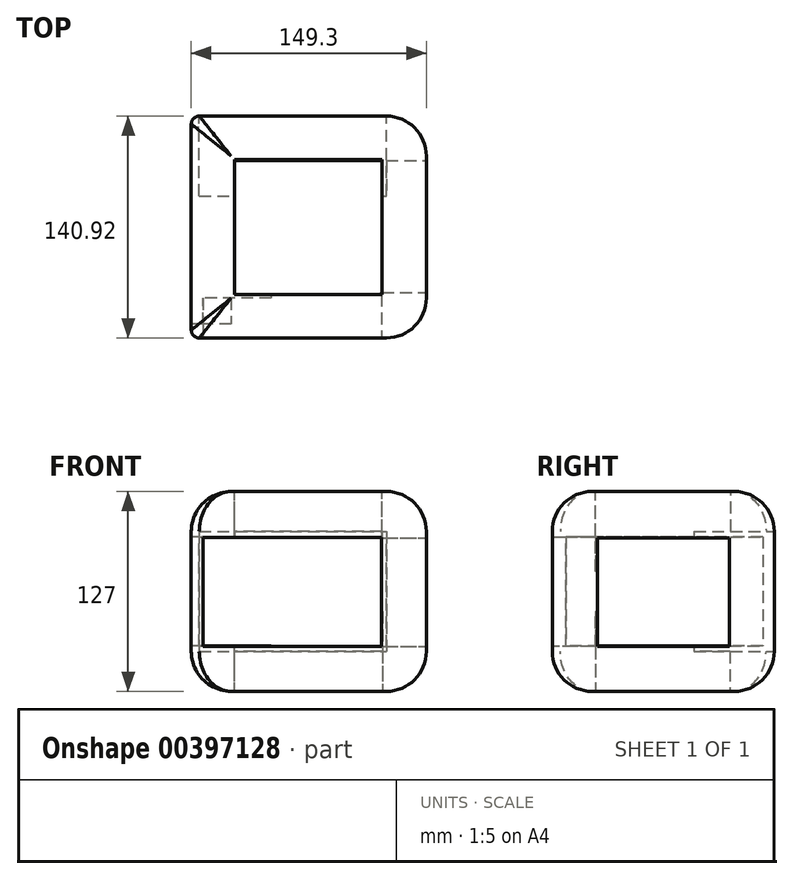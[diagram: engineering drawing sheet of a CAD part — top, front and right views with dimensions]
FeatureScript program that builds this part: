
annotation { "Feature Type Name" : "Feature", "Feature Type Description" : "" }
export const myFeature = defineFeature(function(context is Context, id is Id, definition is map)
    precondition{}
    {
        {
            var Q0;
            Q0=qCreatedBy(makeId("Top.planeOp"),FACE);
            var sketch = newSketch(context, id + "F0", { "sketchPlane" : qUnion([Q0])});
            skLineSegment(sketch, "E0.bottom", {"start": v(-73.46, -68.51) * mm, "end": v(75.84, -68.51) * mm});
            skLineSegment(sketch, "E0.top", {"start": v(-73.46, 72.4) * mm, "end": v(75.84, 72.4) * mm});
            skLineSegment(sketch, "E0.left", {"start": v(-73.46, -68.51) * mm, "end": v(-73.46, 72.4) * mm});
            skLineSegment(sketch, "E0.right", {"start": v(75.84, -68.51) * mm, "end": v(75.84, 72.4) * mm});
            skSolve(sketch);
        }
        {
            var Q0;
            Q0 = qSketchRegion(id + "F0", true);
            extrude(context, id + "F1", {"entities" : qUnion([Q0]), "depth" : 127 * mm});
        }
        {
            var Q0;
            Q0=makeQuery(id+"F1.opExtrude","CAP_EDGE",EDGE,{"disambiguationData":[OSD([sQuery(id+"F0.wireOp",EDGE,"E0.right")])],"isStart":false});
            var Q1;
            Q1=makeQuery(id+"F1.opExtrude","CAP_EDGE",EDGE,{"disambiguationData":[OSD([sQuery(id+"F0.wireOp",EDGE,"E0.top")])],"isStart":false});
            var Q2;
            Q2=makeQuery(id+"F1.opExtrude","CAP_EDGE",EDGE,{"disambiguationData":[OSD([sQuery(id+"F0.wireOp",EDGE,"E0.left")])],"isStart":false});
            var Q3;
            Q3=makeQuery(id+"F1.opExtrude","CAP_EDGE",EDGE,{"disambiguationData":[OSD([sQuery(id+"F0.wireOp",EDGE,"E0.bottom")])],"isStart":false});
            var Q4;
            Q4=makeQuery(id+"F1.opExtrude","CAP_EDGE",EDGE,{"disambiguationData":[OSD([sQuery(id+"F0.wireOp",EDGE,"E0.top")])],"isStart":true});
            var Q5;
            Q5=makeQuery(id+"F1.opExtrude","SWEPT_FACE",FACE,{"disambiguationData":[OSD([sQuery(id+"F0.wireOp",EDGE,"E0.right")])]});
            var Q6;
            Q6=makeQuery(id+"F1.opExtrude","CAP_EDGE",EDGE,{"disambiguationData":[OSD([sQuery(id+"F0.wireOp",EDGE,"E0.bottom")])],"isStart":true});
            var Q7;
            Q7=makeQuery(id+"F1.opExtrude","CAP_EDGE",EDGE,{"disambiguationData":[OSD([sQuery(id+"F0.wireOp",EDGE,"E0.left")])],"isStart":true});
            fillet(context, id + "F2", {"entities" : qUnion([Q0, Q1, Q2, Q3, Q4, Q5, Q6, Q7]), "radius" : 25.4 * mm, "tangentPropagation" : true, "allowEdgeOverflow" : false});
        }
        {
            var Q0;
            Q0=makeQuery(id+"F2.opFillet","BLEND_EDGE",EDGE,{"blendedFrom":[makeQuery(id+"F1.opExtrude","CAP_EDGE",EDGE,{"disambiguationData":[OSD([sQuery(id+"F0.wireOp",EDGE,"E0.top")])],"isStart":false}),makeQuery(id+"F1.opExtrude","CAP_EDGE",EDGE,{"disambiguationData":[OSD([sQuery(id+"F0.wireOp",EDGE,"E0.left")])],"isStart":false})],"blendedInto":[]});
            var Q1;
            Q1=makeQuery(id+"F2.opFillet","BLEND_EDGE",EDGE,{"blendedFrom":[makeQuery(id+"F1.opExtrude","CAP_EDGE",EDGE,{"disambiguationData":[OSD([sQuery(id+"F0.wireOp",EDGE,"E0.bottom")])],"isStart":false}),makeQuery(id+"F1.opExtrude","CAP_EDGE",EDGE,{"disambiguationData":[OSD([sQuery(id+"F0.wireOp",EDGE,"E0.left")])],"isStart":false})],"blendedInto":[]});
            var Q2;
            {var subQ0=sQuery(id+"F0.wireOp",EDGE,"E0.left");Q2=makeQuery(id+"F2.opFillet","BLEND_EDGE",EDGE,{"blendedFrom":[makeQuery(id+"F1.opExtrude","CAP_EDGE",EDGE,{"disambiguationData":[OSD([subQ0])],"isStart":false}),makeQuery(id+"F1.opExtrude","SWEPT_FACE",FACE,{"disambiguationData":[OSD([subQ0])]})],"blendedInto":[makeQuery(id+"F1.opExtrude","SWEPT_FACE",FACE,{"disambiguationData":[OSD([subQ0])]})]});}
            var Q3;
            {var subQ0=sQuery(id+"F0.wireOp",EDGE,"E0.top");Q3=makeQuery(id+"F2.opFillet","BLEND_EDGE",EDGE,{"blendedFrom":[makeQuery(id+"F1.opExtrude","CAP_EDGE",EDGE,{"disambiguationData":[OSD([subQ0])],"isStart":false}),makeQuery(id+"F1.opExtrude","SWEPT_FACE",FACE,{"disambiguationData":[OSD([subQ0])]})],"blendedInto":[makeQuery(id+"F1.opExtrude","SWEPT_FACE",FACE,{"disambiguationData":[OSD([subQ0])]})]});}
            fillet(context, id + "F3", {"entities" : qUnion([Q0, Q1, Q2, Q3]), "radius" : 5.08 * mm, "tangentPropagation" : true, "allowEdgeOverflow" : false});
        }
        {
            var Q0;
            Q0=makeQuery(id+"F1.opExtrude","CAP_FACE",FACE,{"disambiguationData":[OSD([sQuery(id+"F0.wireOp",EDGE,"E0.bottom"),sQuery(id+"F0.wireOp",EDGE,"E0.top"),sQuery(id+"F0.wireOp",EDGE,"E0.left"),sQuery(id+"F0.wireOp",EDGE,"E0.right")])],"isStart":false});
            var sketch = newSketch(context, id + "F4", { "sketchPlane" : qUnion([Q0])});
            skLineSegment(sketch, "E1.bottom", {"start": v(-46, 44.95) * mm, "end": v(47.65, 44.95) * mm});
            skLineSegment(sketch, "E1.top", {"start": v(-46, -40.95) * mm, "end": v(47.65, -40.95) * mm});
            skLineSegment(sketch, "E1.left", {"start": v(-46, 44.95) * mm, "end": v(-46, -40.95) * mm});
            skLineSegment(sketch, "E1.right", {"start": v(47.65, 44.95) * mm, "end": v(47.65, -40.95) * mm});
            skSolve(sketch);
        }
        {
            var Q0;
            Q0 = qSketchRegion(id + "F4", true);
            extrude(context, id + "F5", {"entities" : qUnion([Q0]), "operationType" : NewBodyOperationType.REMOVE, "oppositeDirection" : true, "depth" : 25.4 * mm});
        }
        {
            var Q0;
            Q0=makeQuery(id+"F1.opExtrude","CAP_FACE",FACE,{"disambiguationData":[OSD([sQuery(id+"F0.wireOp",EDGE,"E0.bottom"),sQuery(id+"F0.wireOp",EDGE,"E0.top"),sQuery(id+"F0.wireOp",EDGE,"E0.left"),sQuery(id+"F0.wireOp",EDGE,"E0.right")])],"isStart":true});
            var sketch = newSketch(context, id + "F6", { "sketchPlane" : qUnion([Q0])});
            skLineSegment(sketch, "E2.bottom", {"start": v(-46.24, 40.95) * mm, "end": v(47.89, 40.95) * mm});
            skLineSegment(sketch, "E2.top", {"start": v(-46.24, -44.24) * mm, "end": v(47.89, -44.24) * mm});
            skLineSegment(sketch, "E2.left", {"start": v(-46.24, 40.95) * mm, "end": v(-46.24, -44.24) * mm});
            skLineSegment(sketch, "E2.right", {"start": v(47.89, 40.95) * mm, "end": v(47.89, -44.24) * mm});
            skSolve(sketch);
        }
        {
            var Q0;
            Q0 = qSketchRegion(id + "F6", true);
            extrude(context, id + "F7", {"entities" : qUnion([Q0]), "operationType" : NewBodyOperationType.REMOVE, "oppositeDirection" : true, "depth" : 25.4 * mm});
        }
        {
            var Q0;
            Q0=makeQuery(id+"F1.opExtrude","SWEPT_FACE",FACE,{"disambiguationData":[OSD([sQuery(id+"F0.wireOp",EDGE,"E0.left")])]});
            var sketch = newSketch(context, id + "F8", { "sketchPlane" : qUnion([Q0])});
            skLineSegment(sketch, "E3.bottom", {"start": v(-65.1, 98.2) * mm, "end": v(59.77, 98.2) * mm});
            skLineSegment(sketch, "E3.top", {"start": v(-65.1, 28.85) * mm, "end": v(59.77, 28.85) * mm});
            skLineSegment(sketch, "E3.left", {"start": v(-65.1, 98.2) * mm, "end": v(-65.1, 28.85) * mm});
            skLineSegment(sketch, "E3.right", {"start": v(59.77, 98.2) * mm, "end": v(59.77, 28.85) * mm});
            skSolve(sketch);
        }
        {
            var Q0;
            Q0 = qSketchRegion(id + "F8", true);
            extrude(context, id + "F9", {"entities" : qUnion([Q0]), "operationType" : NewBodyOperationType.REMOVE, "oppositeDirection" : true, "depth" : 25.4 * mm});
        }
        {
            var Q0;
            Q0=makeQuery(id+"F1.opExtrude","SWEPT_FACE",FACE,{"disambiguationData":[OSD([sQuery(id+"F0.wireOp",EDGE,"E0.bottom")])]});
            var sketch = newSketch(context, id + "F10", { "sketchPlane" : qUnion([Q0])});
            skLineSegment(sketch, "E4.bottom", {"start": v(-66.05, 97.88) * mm, "end": v(47.54, 97.88) * mm});
            skLineSegment(sketch, "E4.top", {"start": v(-66.05, 28.54) * mm, "end": v(47.54, 28.54) * mm});
            skLineSegment(sketch, "E4.left", {"start": v(-66.05, 97.88) * mm, "end": v(-66.05, 28.54) * mm});
            skLineSegment(sketch, "E4.right", {"start": v(47.54, 97.88) * mm, "end": v(47.54, 28.54) * mm});
            skSolve(sketch);
        }
        {
            var Q0;
            Q0 = qSketchRegion(id + "F10", true);
            extrude(context, id + "F11", {"entities" : qUnion([Q0]), "operationType" : NewBodyOperationType.REMOVE, "oppositeDirection" : true, "depth" : 25.4 * mm});
        }
        {
            var Q0;
            Q0=makeQuery(id+"F1.opExtrude","SWEPT_FACE",FACE,{"disambiguationData":[OSD([sQuery(id+"F0.wireOp",EDGE,"E0.right")])]});
            var sketch = newSketch(context, id + "F12", { "sketchPlane" : qUnion([Q0])});
            skLineSegment(sketch, "E5.bottom", {"start": v(-39.7, 97.57) * mm, "end": v(44.08, 97.57) * mm});
            skLineSegment(sketch, "E5.top", {"start": v(-39.7, 28.54) * mm, "end": v(44.08, 28.54) * mm});
            skLineSegment(sketch, "E5.left", {"start": v(-39.7, 97.57) * mm, "end": v(-39.7, 28.54) * mm});
            skLineSegment(sketch, "E5.right", {"start": v(44.08, 97.57) * mm, "end": v(44.08, 28.54) * mm});
            skSolve(sketch);
        }
        {
            var Q0;
            Q0 = qSketchRegion(id + "F12", true);
            extrude(context, id + "F13", {"entities" : qUnion([Q0]), "operationType" : NewBodyOperationType.REMOVE, "oppositeDirection" : true, "depth" : 25.4 * mm});
        }
        {
            var Q0;
            Q0=makeQuery(id+"F5.boolean.opBoolean","COPY",FACE,{"derivedFrom":makeQuery(id+"F5.opExtrude","CAP_FACE",FACE,{"disambiguationData":[OSD([sQuery(id+"F4.wireOp",EDGE,"E1.bottom"),sQuery(id+"F4.wireOp",EDGE,"E1.top"),sQuery(id+"F4.wireOp",EDGE,"E1.left"),sQuery(id+"F4.wireOp",EDGE,"E1.right")])],"isStart":false})});
            var sketch = newSketch(context, id + "F14", { "sketchPlane" : qUnion([Q0])});
            skLineSegment(sketch, "E6.bottom", {"start": v(-46, 44.95) * mm, "end": v(47.65, 44.95) * mm});
            skLineSegment(sketch, "E6.top", {"start": v(-46, -40.95) * mm, "end": v(47.65, -40.95) * mm});
            skLineSegment(sketch, "E6.left", {"start": v(-46, 44.95) * mm, "end": v(-46, -40.95) * mm});
            skLineSegment(sketch, "E6.right", {"start": v(47.65, 44.95) * mm, "end": v(47.65, -40.95) * mm});
            skSolve(sketch);
        }
        {
            var Q0;
            Q0 = qSketchRegion(id + "F14", true);
            extrude(context, id + "F15", {"entities" : qUnion([Q0]), "operationType" : NewBodyOperationType.REMOVE, "oppositeDirection" : true, "depth" : 25.4 * mm});
        }
        {
            var Q0;
            Q0=makeQuery(id+"F7.boolean.opBoolean","COPY",FACE,{"derivedFrom":makeQuery(id+"F7.opExtrude","CAP_FACE",FACE,{"disambiguationData":[OSD([sQuery(id+"F6.wireOp",EDGE,"E2.bottom"),sQuery(id+"F6.wireOp",EDGE,"E2.top"),sQuery(id+"F6.wireOp",EDGE,"E2.left"),sQuery(id+"F6.wireOp",EDGE,"E2.right")])],"isStart":false})});
            var sketch = newSketch(context, id + "F16", { "sketchPlane" : qUnion([Q0])});
            skLineSegment(sketch, "E7.bottom", {"start": v(-46.24, 40.95) * mm, "end": v(47.89, 40.95) * mm});
            skLineSegment(sketch, "E7.top", {"start": v(-46.24, -44.24) * mm, "end": v(47.89, -44.24) * mm});
            skLineSegment(sketch, "E7.left", {"start": v(-46.24, 40.95) * mm, "end": v(-46.24, -44.24) * mm});
            skLineSegment(sketch, "E7.right", {"start": v(47.89, 40.95) * mm, "end": v(47.89, -44.24) * mm});
            skSolve(sketch);
        }
        {
            var Q0;
            Q0 = qSketchRegion(id + "F16", true);
            extrude(context, id + "F17", {"entities" : qUnion([Q0]), "operationType" : NewBodyOperationType.REMOVE, "oppositeDirection" : true, "depth" : 25.4 * mm});
        }
        {
            var Q0;
            Q0=makeQuery(id+"F9.boolean.opBoolean","COPY",FACE,{"derivedFrom":makeQuery(id+"F9.opExtrude","CAP_FACE",FACE,{"disambiguationData":[OSD([sQuery(id+"F8.wireOp",EDGE,"E3.bottom"),sQuery(id+"F8.wireOp",EDGE,"E3.top"),sQuery(id+"F8.wireOp",EDGE,"E3.left"),sQuery(id+"F8.wireOp",EDGE,"E3.right")])],"isStart":false})});
            var sketch = newSketch(context, id + "F18", { "sketchPlane" : qUnion([Q0])});
            skLineSegment(sketch, "E8.bottom", {"start": v(-65.1, 98.2) * mm, "end": v(43.11, 98.2) * mm});
            skLineSegment(sketch, "E8.top", {"start": v(-65.1, 28.85) * mm, "end": v(43.11, 28.85) * mm});
            skLineSegment(sketch, "E8.left", {"start": v(-65.1, 98.2) * mm, "end": v(-65.1, 28.85) * mm});
            skLineSegment(sketch, "E8.right", {"start": v(43.11, 98.2) * mm, "end": v(43.11, 28.85) * mm});
            skSolve(sketch);
        }
        {
            var Q0;
            Q0 = qSketchRegion(id + "F18", true);
            extrude(context, id + "F19", {"entities" : qUnion([Q0]), "operationType" : NewBodyOperationType.REMOVE, "oppositeDirection" : true, "depth" : 25.4 * mm});
        }
        {
            var Q0;
            Q0=makeQuery(id+"F1.opExtrude","SWEPT_FACE",FACE,{"disambiguationData":[OSD([sQuery(id+"F0.wireOp",EDGE,"E0.top")])]});
            var sketch = newSketch(context, id + "F20", { "sketchPlane" : qUnion([Q0])});
            skLineSegment(sketch, "E9.bottom", {"start": v(-50.44, 101.6) * mm, "end": v(68.38, 101.6) * mm});
            skLineSegment(sketch, "E9.top", {"start": v(-50.44, 25.4) * mm, "end": v(68.38, 25.4) * mm});
            skLineSegment(sketch, "E9.left", {"start": v(-50.44, 101.6) * mm, "end": v(-50.44, 25.4) * mm});
            skLineSegment(sketch, "E9.right", {"start": v(68.38, 101.6) * mm, "end": v(68.38, 25.4) * mm});
            skSolve(sketch);
        }
        {
            var Q0;
            Q0 = qSketchRegion(id + "F20", true);
            extrude(context, id + "F21", {"entities" : qUnion([Q0]), "operationType" : NewBodyOperationType.REMOVE, "oppositeDirection" : true, "depth" : 25.4 * mm});
        }
        {
            var Q0;
            Q0=makeQuery(id+"F13.boolean.opBoolean","COPY",FACE,{"derivedFrom":makeQuery(id+"F13.opExtrude","CAP_FACE",FACE,{"disambiguationData":[OSD([sQuery(id+"F12.wireOp",EDGE,"E5.bottom"),sQuery(id+"F12.wireOp",EDGE,"E5.top"),sQuery(id+"F12.wireOp",EDGE,"E5.left"),sQuery(id+"F12.wireOp",EDGE,"E5.right")])],"isStart":false})});
            var sketch = newSketch(context, id + "F22", { "sketchPlane" : qUnion([Q0])});
            skLineSegment(sketch, "E10.bottom", {"start": v(-39.7, 97.57) * mm, "end": v(44.08, 97.57) * mm});
            skLineSegment(sketch, "E10.top", {"start": v(-39.7, 28.54) * mm, "end": v(44.08, 28.54) * mm});
            skLineSegment(sketch, "E10.left", {"start": v(-39.7, 97.57) * mm, "end": v(-39.7, 28.54) * mm});
            skLineSegment(sketch, "E10.right", {"start": v(44.08, 97.57) * mm, "end": v(44.08, 28.54) * mm});
            skSolve(sketch);
        }
        {
            var Q0;
            Q0 = qSketchRegion(id + "F22", true);
            extrude(context, id + "F23", {"entities" : qUnion([Q0]), "operationType" : NewBodyOperationType.REMOVE, "oppositeDirection" : true, "depth" : 25.4 * mm});
        }
        {
            var Q0;
            Q0=makeQuery(id+"F11.boolean.opBoolean","COPY",FACE,{"derivedFrom":makeQuery(id+"F11.opExtrude","CAP_FACE",FACE,{"disambiguationData":[OSD([sQuery(id+"F10.wireOp",EDGE,"E4.bottom"),sQuery(id+"F10.wireOp",EDGE,"E4.top"),sQuery(id+"F10.wireOp",EDGE,"E4.left"),sQuery(id+"F10.wireOp",EDGE,"E4.right")])],"isStart":false})});
            var sketch = newSketch(context, id + "F24", { "sketchPlane" : qUnion([Q0])});
            skLineSegment(sketch, "E11.bottom", {"start": v(-22.66, 97.88) * mm, "end": v(47.54, 97.88) * mm});
            skLineSegment(sketch, "E11.top", {"start": v(-22.66, 28.54) * mm, "end": v(47.54, 28.54) * mm});
            skLineSegment(sketch, "E11.left", {"start": v(-22.66, 97.88) * mm, "end": v(-22.66, 28.54) * mm});
            skLineSegment(sketch, "E11.right", {"start": v(47.54, 97.88) * mm, "end": v(47.54, 28.54) * mm});
            skSolve(sketch);
        }
        {
            var Q0;
            Q0 = qSketchRegion(id + "F24", true);
            extrude(context, id + "F25", {"entities" : qUnion([Q0]), "operationType" : NewBodyOperationType.REMOVE, "oppositeDirection" : true, "depth" : 25.4 * mm});
        }
        {
            var Q0;
            Q0=makeQuery(id+"F21.boolean.opBoolean","COPY",FACE,{"derivedFrom":makeQuery(id+"F21.opExtrude","CAP_FACE",FACE,{"disambiguationData":[OSD([sQuery(id+"F20.wireOp",EDGE,"E9.bottom"),sQuery(id+"F20.wireOp",EDGE,"E9.top"),sQuery(id+"F20.wireOp",EDGE,"E9.left"),sQuery(id+"F20.wireOp",EDGE,"E9.right")])],"isStart":false})});
            var sketch = newSketch(context, id + "F26", { "sketchPlane" : qUnion([Q0])});
            skLineSegment(sketch, "E12.bottom", {"start": v(-50.44, 101.6) * mm, "end": v(68.38, 101.6) * mm});
            skLineSegment(sketch, "E12.top", {"start": v(-50.44, 25.4) * mm, "end": v(68.38, 25.4) * mm});
            skLineSegment(sketch, "E12.left", {"start": v(-50.44, 101.6) * mm, "end": v(-50.44, 25.4) * mm});
            skLineSegment(sketch, "E12.right", {"start": v(68.38, 101.6) * mm, "end": v(68.38, 25.4) * mm});
            skSolve(sketch);
        }
        {
            var Q0;
            Q0 = qSketchRegion(id + "F26", true);
            extrude(context, id + "F27", {"entities" : qUnion([Q0]), "operationType" : NewBodyOperationType.REMOVE, "oppositeDirection" : true, "depth" : 25.4 * mm});
        }
        {
            var Q0;
            Q0=makeQuery(id+"F27.boolean.opBoolean","COPY",FACE,{"disambiguationData":[TD([makeQuery(id+"F15.boolean.opBoolean","COPY",FACE,{"derivedFrom":makeQuery(id+"F15.opExtrude","CAP_FACE",FACE,{"disambiguationData":[OSD([sQuery(id+"F14.wireOp",EDGE,"E6.bottom"),sQuery(id+"F14.wireOp",EDGE,"E6.top"),sQuery(id+"F14.wireOp",EDGE,"E6.left"),sQuery(id+"F14.wireOp",EDGE,"E6.right")])],"isStart":false})})])],"derivedFrom":makeQuery(id+"F27.opExtrude","CAP_FACE",FACE,{"disambiguationData":[OSD([sQuery(id+"F26.wireOp",EDGE,"E12.bottom"),sQuery(id+"F26.wireOp",EDGE,"E12.top"),sQuery(id+"F26.wireOp",EDGE,"E12.left"),sQuery(id+"F26.wireOp",EDGE,"E12.right")])],"isStart":false})});
            var sketch = newSketch(context, id + "F28", { "sketchPlane" : qUnion([Q0])});
            skLineSegment(sketch, "E13.bottom", {"start": v(-25.04, 76.2) * mm, "end": v(22.66, 76.2) * mm});
            skLineSegment(sketch, "E13.top", {"start": v(-25.04, 50.8) * mm, "end": v(22.66, 50.8) * mm});
            skLineSegment(sketch, "E13.left", {"start": v(-25.04, 76.2) * mm, "end": v(-25.04, 50.8) * mm});
            skLineSegment(sketch, "E13.right", {"start": v(22.66, 76.2) * mm, "end": v(22.66, 50.8) * mm});
            skSolve(sketch);
        }
        {
            var Q0;
            Q0 = qSketchRegion(id + "F28", true);
            extrude(context, id + "F29", {"entities" : qUnion([Q0]), "operationType" : NewBodyOperationType.REMOVE, "oppositeDirection" : true, "depth" : 25.4 * mm});
        }
        {
            var Q0;
            Q0=makeQuery(id+"F29.boolean.opBoolean","COPY",FACE,{"derivedFrom":makeQuery(id+"F29.opExtrude","CAP_FACE",FACE,{"disambiguationData":[OSD([sQuery(id+"F28.wireOp",EDGE,"E13.bottom"),sQuery(id+"F28.wireOp",EDGE,"E13.top"),sQuery(id+"F28.wireOp",EDGE,"E13.left"),sQuery(id+"F28.wireOp",EDGE,"E13.right")])],"isStart":false})});
            var sketch = newSketch(context, id + "F30", { "sketchPlane" : qUnion([Q0])});
            skLineSegment(sketch, "E14.bottom", {"start": v(-25.04, 76.2) * mm, "end": v(22.66, 76.2) * mm});
            skLineSegment(sketch, "E14.top", {"start": v(-25.04, 50.8) * mm, "end": v(22.66, 50.8) * mm});
            skLineSegment(sketch, "E14.left", {"start": v(-25.04, 76.2) * mm, "end": v(-25.04, 50.8) * mm});
            skLineSegment(sketch, "E14.right", {"start": v(22.66, 76.2) * mm, "end": v(22.66, 50.8) * mm});
            skSolve(sketch);
        }
        {
            var Q0;
            Q0 = qSketchRegion(id + "F30", true);
            extrude(context, id + "F31", {"entities" : qUnion([Q0]), "operationType" : NewBodyOperationType.REMOVE, "oppositeDirection" : true, "depth" : 25.4 * mm});
        }
    });
